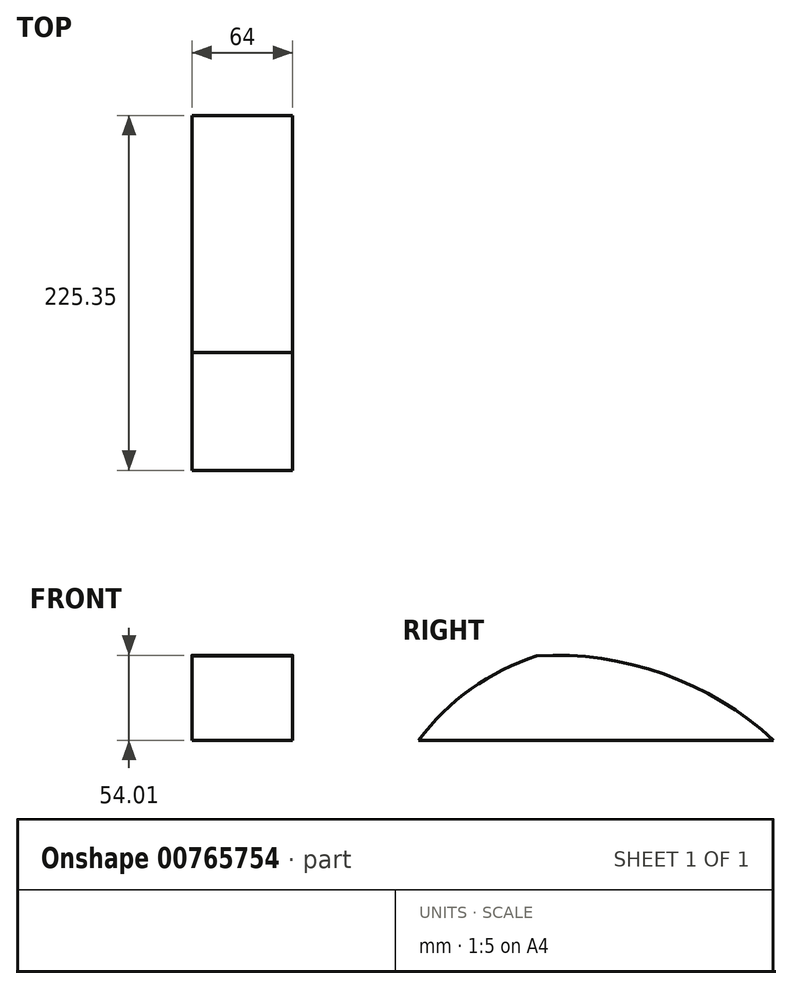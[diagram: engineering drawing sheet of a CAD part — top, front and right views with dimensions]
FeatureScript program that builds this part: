
annotation { "Feature Type Name" : "Feature", "Feature Type Description" : "" }
export const myFeature = defineFeature(function(context is Context, id is Id, definition is map)
    precondition{}
    {
        {
            var Q0;
            Q0=qCreatedBy(makeId("Right.planeOp"),FACE);
            var sketch = newSketch(context, id + "F0", { "sketchPlane" : qUnion([Q0])});
            skLineSegment(sketch, "E0.bottom", {"start": v(-74.96, 0) * mm, "end": v(150.39, 0) * mm});
            skLineSegment(sketch, "E0.top", {"start": v(-74.96, -86.22) * mm, "end": v(150.39, -86.22) * mm});
            skLineSegment(sketch, "E0.left", {"start": v(-74.96, 0) * mm, "end": v(-74.96, -86.22) * mm});
            skLineSegment(sketch, "E0.right", {"start": v(150.39, 0) * mm, "end": v(150.39, -86.22) * mm});
            skSolve(sketch);
        }
        {
            var Q0;
            Q0 = qSketchRegion(id + "F0", true);
            extrude(context, id + "F1", {"entities" : qUnion([Q0]), "oppositeDirection" : true, "depth" : 64 * mm, "offsetDistance" : 25 * mm});
        }
        {
            var Q0;
            Q0=makeQuery(id+"F1.opExtrude","CAP_FACE",FACE,{"disambiguationData":[OSD([sQuery(id+"F0.wireOp",EDGE,"E0.bottom"),sQuery(id+"F0.wireOp",EDGE,"E0.top"),sQuery(id+"F0.wireOp",EDGE,"E0.left"),sQuery(id+"F0.wireOp",EDGE,"E0.right")])],"isStart":true});
            var sketch = newSketch(context, id + "F2", { "sketchPlane" : qUnion([Q0])});
            skArc(sketch, "E1", {"start": v(0, -32.58) * mm, "mid": v(-41.68, -53.53) * mm, "end": v(-74.96, -86.22) * mm});
            skArc(sketch, "E2", {"start": v(0, 0) * mm, "mid": v(45.85, -94.3) * mm, "end": v(150.39, -86.22) * mm});
            skArc(sketch, "E3", {"start": v(150.39, -86.22) * mm, "mid": v(80.67, -44.04) * mm, "end": v(0, -32.58) * mm});
            skSolve(sketch);
        }
        {
            var Q0;
            {var subQ5=makeQuery(id+"F1.opExtrude","CAP_EDGE",EDGE,{"disambiguationData":[OSD([sQuery(id+"F0.wireOp",EDGE,"E0.right")])],"isStart":true});Q0=makeQuery(id+"F2.imprint","IMPRINT",FACE,{"disambiguationData":[TD([[makeQuery(id+"F2.imprint","IMPRINT",EDGE,{"derivedFrom":subQ5}),-1.0]])]});}
            var Q1;
            {var subQ6=sQuery(id+"F2.wireOp",EDGE,"E1");Q1=makeQuery(id+"F2.imprint","IMPRINT",FACE,{"disambiguationData":[TD([[makeQuery(id+"F2.imprint","IMPRINT",EDGE,{"derivedFrom":subQ6}),-1.0]])]});}
            extrude(context, id + "F3", {"entities" : qUnion([Q0, Q1]), "operationType" : NewBodyOperationType.REMOVE, "endBound" : BoundingType.THROUGH_ALL, "oppositeDirection" : true, "depth" : 25 * mm, "offsetDistance" : 25 * mm});
        }
    });
